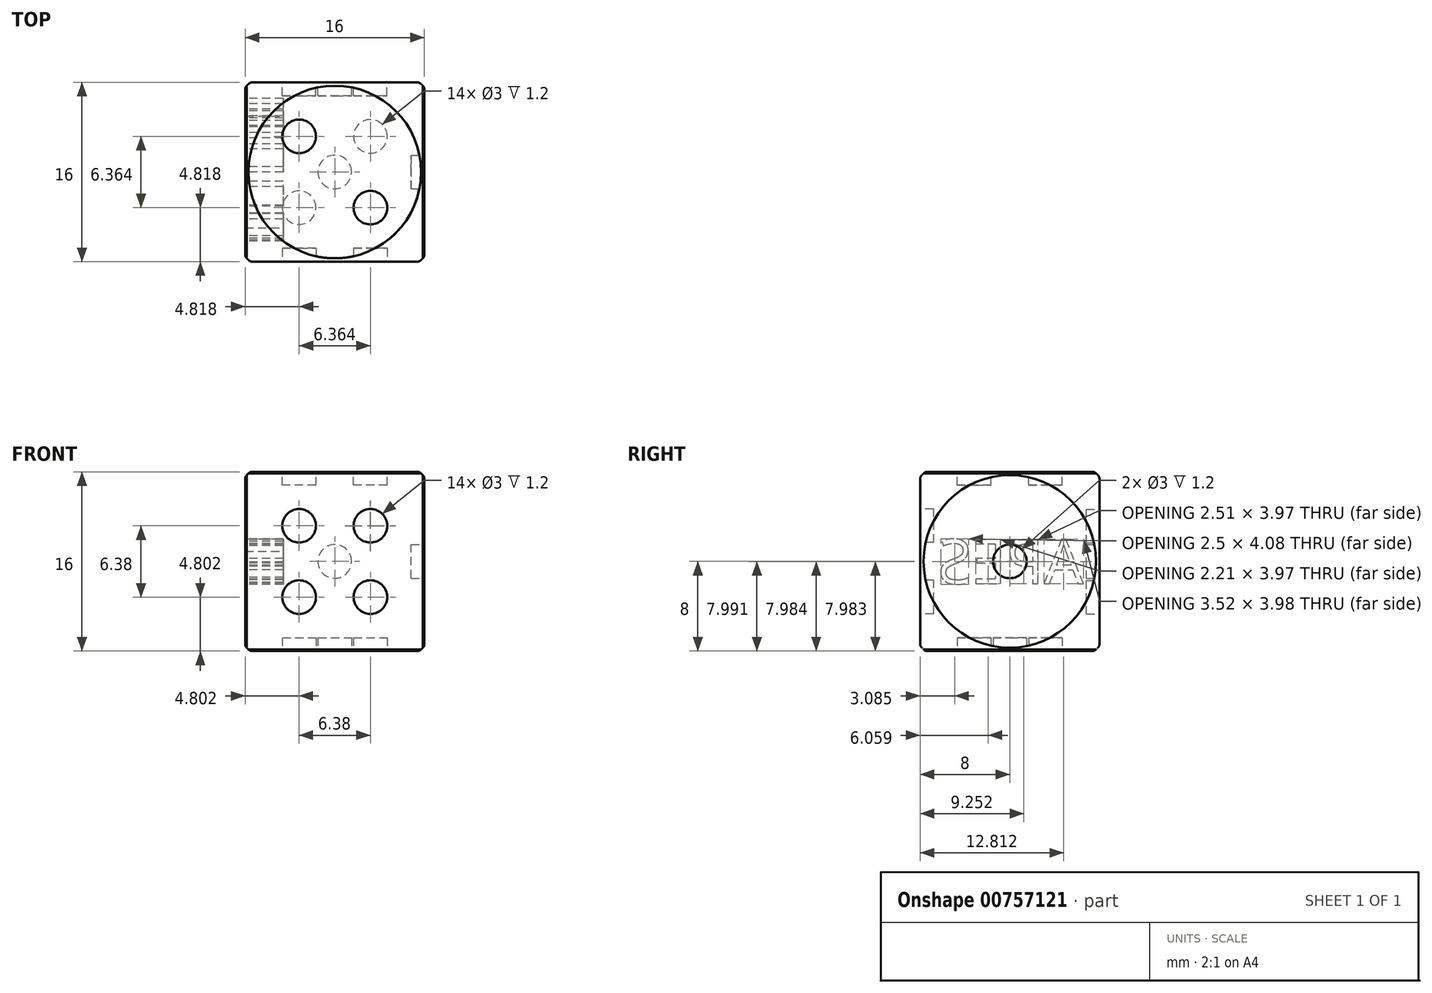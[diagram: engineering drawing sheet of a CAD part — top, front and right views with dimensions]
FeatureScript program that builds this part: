
annotation { "Feature Type Name" : "Feature", "Feature Type Description" : "" }
export const myFeature = defineFeature(function(context is Context, id is Id, definition is map)
    precondition{}
    {
        {
            var Q0;
            Q0=qCreatedBy(makeId("Top.planeOp"),FACE);
            var sketch = newSketch(context, id + "F0", { "sketchPlane" : qUnion([Q0])});
            skLineSegment(sketch, "E0.bottom", {"start": v(-8, 8) * mm, "end": v(8, 8) * mm});
            skLineSegment(sketch, "E0.top", {"start": v(-8, -8) * mm, "end": v(8, -8) * mm});
            skLineSegment(sketch, "E0.left", {"start": v(-8, 8) * mm, "end": v(-8, -8) * mm});
            skLineSegment(sketch, "E0.right", {"start": v(8, 8) * mm, "end": v(8, -8) * mm});
            skSolve(sketch);
        }
        {
            var Q0;
            Q0=makeQuery(id+"F0.imprint","IMPRINT",FACE,{"disambiguationData":[TD([[makeQuery(id+"F0.imprint","IMPRINT",EDGE,{"derivedFrom":sQuery(id+"F0.wireOp",EDGE,"E0.bottom")}),-1.0]])]});
            extrude(context, id + "F1", {"entities" : qUnion([Q0]), "endBound" : BoundingType.SYMMETRIC, "depth" : 16 * mm, "offsetDistance" : 25 * mm});
        }
        {
            var Q0;
            Q0=qCreatedBy(makeId("Top.planeOp"),FACE);
            var sketch = newSketch(context, id + "F2", { "sketchPlane" : qUnion([Q0])});
            skArc(sketch, "E1", {"start": v(0, 11) * mm, "mid": v(-11, 0) * mm, "end": v(0, -11) * mm});
            skLineSegment(sketch, "E2", {"start": v(0, 11) * mm, "end": v(0, 18.89) * mm});
            skArc(sketch, "E3", {"start": v(0, 18.89) * mm, "mid": v(-18.89, 0) * mm, "end": v(0, -18.89) * mm});
            skLineSegment(sketch, "E4", {"start": v(0, -11) * mm, "end": v(0, -18.89) * mm});
            skLineSegment(sketch, "E5", {"start": v(0, 33.4) * mm, "end": v(0, -38.28) * mm, "construction": true});
            skSolve(sketch);
        }
        {
            var Q0;
            Q0=makeQuery(id+"F2.imprint","IMPRINT",FACE,{"disambiguationData":[TD([[makeQuery(id+"F2.imprint","IMPRINT",EDGE,{"derivedFrom":sQuery(id+"F2.wireOp",EDGE,"E1")}),-1.0]])]});
            var Q1;
            Q1=sQuery(id+"F2.wireOp",EDGE,"E5");
            revolve(context, id + "F3", {"operationType" : NewBodyOperationType.REMOVE, "surfaceOperationType" : NewSurfaceOperationType.NEW, "entities" : qUnion([Q0]), "axis" : qUnion([Q1]), "revolveType" : RevolveType.FULL});
        }
        {
            var Q0;
            Q0=makeQuery(id+"F1.opExtrude","CAP_FACE",FACE,{"disambiguationData":[OSD([sQuery(id+"F0.wireOp",EDGE,"E0.bottom"),sQuery(id+"F0.wireOp",EDGE,"E0.top"),sQuery(id+"F0.wireOp",EDGE,"E0.left"),sQuery(id+"F0.wireOp",EDGE,"E0.right")])],"isStart":false});
            var Q1;
            Q1=makeQuery(id+"F1.opExtrude","SWEPT_FACE",FACE,{"disambiguationData":[OSD([sQuery(id+"F0.wireOp",EDGE,"E0.top")])]});
            var Q2;
            Q2=makeQuery(id+"F1.opExtrude","SWEPT_FACE",FACE,{"disambiguationData":[OSD([sQuery(id+"F0.wireOp",EDGE,"E0.left")])]});
            var Q3;
            Q3=makeQuery(id+"F1.opExtrude","SWEPT_FACE",FACE,{"disambiguationData":[OSD([sQuery(id+"F0.wireOp",EDGE,"E0.right")])]});
            var Q4;
            Q4=makeQuery(id+"F1.opExtrude","SWEPT_FACE",FACE,{"disambiguationData":[OSD([sQuery(id+"F0.wireOp",EDGE,"E0.bottom")])]});
            var Q5;
            Q5=makeQuery(id+"F1.opExtrude","CAP_FACE",FACE,{"disambiguationData":[OSD([sQuery(id+"F0.wireOp",EDGE,"E0.bottom"),sQuery(id+"F0.wireOp",EDGE,"E0.top"),sQuery(id+"F0.wireOp",EDGE,"E0.left"),sQuery(id+"F0.wireOp",EDGE,"E0.right")])],"isStart":true});
            fillet(context, id + "F4", {"entities" : qUnion([Q0, Q1, Q2, Q3, Q4, Q5]), "radius" : 0.5 * mm, "tangentPropagation" : true, "allowEdgeOverflow" : false});
        }
        {
            var Q0;
            Q0=makeQuery(id+"F1.opExtrude","CAP_FACE",FACE,{"disambiguationData":[OSD([sQuery(id+"F0.wireOp",EDGE,"E0.bottom"),sQuery(id+"F0.wireOp",EDGE,"E0.top"),sQuery(id+"F0.wireOp",EDGE,"E0.left"),sQuery(id+"F0.wireOp",EDGE,"E0.right")])],"isStart":false});
            var sketch = newSketch(context, id + "F5", { "sketchPlane" : qUnion([Q0])});
            skLineSegment(sketch, "E6", {"start": v(-6.8, 6.8) * mm, "end": v(0, 0) * mm, "construction": true});
            skLineSegment(sketch, "E7", {"start": v(0, 0) * mm, "end": v(6.37, -6.37) * mm, "construction": true});
            skCircle(sketch, "E8", {"center": v(-3.18, 3.18) * mm, "radius": 1.5 * mm});
            skCircle(sketch, "E9", {"center": v(3.18, -3.18) * mm, "radius": 1.5 * mm});
            skSolve(sketch);
        }
        {
            var Q0;
            Q0 = qSketchRegion(id + "F5", true);
            extrude(context, id + "F6", {"entities" : qUnion([Q0]), "operationType" : NewBodyOperationType.REMOVE, "oppositeDirection" : true, "depth" : 1.2 * mm, "offsetDistance" : 25 * mm});
        }
        {
            var Q0;
            Q0=makeQuery(id+"F1.opExtrude","SWEPT_FACE",FACE,{"disambiguationData":[OSD([sQuery(id+"F0.wireOp",EDGE,"E0.right")])]});
            var sketch = newSketch(context, id + "F7", { "sketchPlane" : qUnion([Q0])});
            skCircle(sketch, "E10", {"center": v(0, 0) * mm, "radius": 1.5 * mm});
            skSolve(sketch);
        }
        {
            var Q0;
            Q0 = qSketchRegion(id + "F7", true);
            extrude(context, id + "F8", {"entities" : qUnion([Q0]), "operationType" : NewBodyOperationType.REMOVE, "oppositeDirection" : true, "depth" : 1.2 * mm, "offsetDistance" : 25 * mm});
        }
        {
            var Q0;
            Q0=makeQuery(id+"F1.opExtrude","CAP_FACE",FACE,{"disambiguationData":[OSD([sQuery(id+"F0.wireOp",EDGE,"E0.bottom"),sQuery(id+"F0.wireOp",EDGE,"E0.top"),sQuery(id+"F0.wireOp",EDGE,"E0.left"),sQuery(id+"F0.wireOp",EDGE,"E0.right")])],"isStart":true});
            var sketch = newSketch(context, id + "F9", { "sketchPlane" : qUnion([Q0])});
            skLineSegment(sketch, "E11", {"start": v(0, 0) * mm, "end": v(-3.18, 3.18) * mm, "construction": true});
            skLineSegment(sketch, "E12", {"start": v(0, 0) * mm, "end": v(3.18, -3.18) * mm, "construction": true});
            skLineSegment(sketch, "E13", {"start": v(0, 0) * mm, "end": v(3.18, 3.18) * mm, "construction": true});
            skLineSegment(sketch, "E14", {"start": v(0, 0) * mm, "end": v(-3.18, -3.18) * mm, "construction": true});
            skCircle(sketch, "E15", {"center": v(-3.18, 3.18) * mm, "radius": 1.5 * mm});
            skCircle(sketch, "E16", {"center": v(3.18, 3.18) * mm, "radius": 1.5 * mm});
            skCircle(sketch, "E17", {"center": v(-3.18, -3.18) * mm, "radius": 1.5 * mm});
            skCircle(sketch, "E18", {"center": v(3.18, -3.18) * mm, "radius": 1.5 * mm});
            skCircle(sketch, "E19", {"center": v(0, 0) * mm, "radius": 1.5 * mm});
            skSolve(sketch);
        }
        {
            var Q0;
            Q0=makeQuery(id+"F9.imprint","IMPRINT",FACE,{"disambiguationData":[TD([[makeQuery(id+"F9.imprint","IMPRINT",EDGE,{"derivedFrom":sQuery(id+"F9.wireOp",EDGE,"E15")}),1.0]])]});
            var Q1;
            Q1=makeQuery(id+"F9.imprint","IMPRINT",FACE,{"disambiguationData":[TD([[makeQuery(id+"F9.imprint","IMPRINT",EDGE,{"derivedFrom":sQuery(id+"F9.wireOp",EDGE,"E19")}),1.0]])]});
            var Q2;
            Q2=makeQuery(id+"F9.imprint","IMPRINT",FACE,{"disambiguationData":[TD([[makeQuery(id+"F9.imprint","IMPRINT",EDGE,{"derivedFrom":sQuery(id+"F9.wireOp",EDGE,"E16")}),1.0]])]});
            var Q3;
            Q3=makeQuery(id+"F9.imprint","IMPRINT",FACE,{"disambiguationData":[TD([[makeQuery(id+"F9.imprint","IMPRINT",EDGE,{"derivedFrom":sQuery(id+"F9.wireOp",EDGE,"E18")}),1.0]])]});
            var Q4;
            Q4=makeQuery(id+"F9.imprint","IMPRINT",FACE,{"disambiguationData":[TD([[makeQuery(id+"F9.imprint","IMPRINT",EDGE,{"derivedFrom":sQuery(id+"F9.wireOp",EDGE,"E17")}),1.0]])]});
            var Q5;
            Q5=sQuery(id+"F9.wireOp",EDGE,"E15");
            var Q6;
            Q6=sQuery(id+"F9.wireOp",EDGE,"E19");
            var Q7;
            Q7=sQuery(id+"F9.wireOp",EDGE,"E16");
            var Q8;
            Q8=sQuery(id+"F9.wireOp",EDGE,"E18");
            var Q9;
            Q9=sQuery(id+"F9.wireOp",EDGE,"E17");
            extrude(context, id + "F10", {"entities" : qUnion([Q0, Q1, Q2, Q3, Q4]), "operationType" : NewBodyOperationType.REMOVE, "surfaceEntities" : qUnion([Q5, Q6, Q7, Q8, Q9]), "oppositeDirection" : true, "depth" : 1.2 * mm, "offsetDistance" : 25 * mm});
        }
        {
            var Q0;
            Q0=makeQuery(id+"F1.opExtrude","SWEPT_FACE",FACE,{"disambiguationData":[OSD([sQuery(id+"F0.wireOp",EDGE,"E0.top")])]});
            var sketch = newSketch(context, id + "F11", { "sketchPlane" : qUnion([Q0])});
            skCircle(sketch, "E20", {"center": v(0, 0) * mm, "radius": 4.5 * mm, "construction": true});
            skLineSegment(sketch, "E21", {"start": v(-4.77, 4.77) * mm, "end": v(4.83, -4.83) * mm, "construction": true});
            skLineSegment(sketch, "E22", {"start": v(4.67, 4.67) * mm, "end": v(-4.7, -4.7) * mm, "construction": true});
            skCircle(sketch, "E23", {"center": v(-3.18, 3.18) * mm, "radius": 1.5 * mm});
            skCircle(sketch, "E24", {"center": v(3.18, 3.18) * mm, "radius": 1.5 * mm});
            skCircle(sketch, "E25", {"center": v(3.18, -3.18) * mm, "radius": 1.5 * mm});
            skCircle(sketch, "E26", {"center": v(-3.18, -3.18) * mm, "radius": 1.5 * mm});
            skSolve(sketch);
        }
        {
            var Q0;
            Q0=makeQuery(id+"F11.imprint","IMPRINT",FACE,{"disambiguationData":[TD([[makeQuery(id+"F11.imprint","IMPRINT",EDGE,{"derivedFrom":sQuery(id+"F11.wireOp",EDGE,"E23")}),1.0]])]});
            var Q1;
            Q1=makeQuery(id+"F11.imprint","IMPRINT",FACE,{"disambiguationData":[TD([[makeQuery(id+"F11.imprint","IMPRINT",EDGE,{"derivedFrom":sQuery(id+"F11.wireOp",EDGE,"E24")}),1.0]])]});
            var Q2;
            Q2=makeQuery(id+"F11.imprint","IMPRINT",FACE,{"disambiguationData":[TD([[makeQuery(id+"F11.imprint","IMPRINT",EDGE,{"derivedFrom":sQuery(id+"F11.wireOp",EDGE,"E25")}),1.0]])]});
            var Q3;
            Q3=makeQuery(id+"F11.imprint","IMPRINT",FACE,{"disambiguationData":[TD([[makeQuery(id+"F11.imprint","IMPRINT",EDGE,{"derivedFrom":sQuery(id+"F11.wireOp",EDGE,"E26")}),1.0]])]});
            extrude(context, id + "F12", {"entities" : qUnion([Q0, Q1, Q2, Q3]), "operationType" : NewBodyOperationType.REMOVE, "oppositeDirection" : true, "depth" : 1.2 * mm, "offsetDistance" : 25 * mm});
        }
        {
            var Q0;
            Q0=makeQuery(id+"F1.opExtrude","SWEPT_FACE",FACE,{"disambiguationData":[OSD([sQuery(id+"F0.wireOp",EDGE,"E0.bottom")])]});
            var sketch = newSketch(context, id + "F13", { "sketchPlane" : qUnion([Q0])});
            skLineSegment(sketch, "E27", {"start": v(-3.17, 3.17) * mm, "end": v(3.2, -3.2) * mm, "construction": true});
            skCircle(sketch, "E28", {"center": v(-3.17, 3.17) * mm, "radius": 1.5 * mm});
            skCircle(sketch, "E29", {"center": v(3.2, -3.2) * mm, "radius": 1.5 * mm});
            skCircle(sketch, "E30", {"center": v(0, 0) * mm, "radius": 1.5 * mm});
            skSolve(sketch);
        }
        {
            var Q0;
            Q0=makeQuery(id+"F13.imprint","IMPRINT",FACE,{"disambiguationData":[TD([[makeQuery(id+"F13.imprint","IMPRINT",EDGE,{"derivedFrom":sQuery(id+"F13.wireOp",EDGE,"E28")}),1.0]])]});
            var Q1;
            Q1=makeQuery(id+"F13.imprint","IMPRINT",FACE,{"disambiguationData":[TD([[makeQuery(id+"F13.imprint","IMPRINT",EDGE,{"derivedFrom":sQuery(id+"F13.wireOp",EDGE,"E30")}),1.0]])]});
            var Q2;
            Q2=makeQuery(id+"F13.imprint","IMPRINT",FACE,{"disambiguationData":[TD([[makeQuery(id+"F13.imprint","IMPRINT",EDGE,{"derivedFrom":sQuery(id+"F13.wireOp",EDGE,"E29")}),1.0]])]});
            extrude(context, id + "F14", {"entities" : qUnion([Q0, Q1, Q2]), "operationType" : NewBodyOperationType.REMOVE, "oppositeDirection" : true, "depth" : 1.2 * mm, "offsetDistance" : 25 * mm});
        }
        {
            var Q0;
            Q0=makeQuery(id+"F1.opExtrude","SWEPT_FACE",FACE,{"disambiguationData":[OSD([sQuery(id+"F0.wireOp",EDGE,"E0.left")])]});
            var sketch = newSketch(context, id + "F15", { "sketchPlane" : qUnion([Q0])});
            skText(sketch, "E31", { "text": "APES", "fontName": "OpenSans-Regular.ttf"});
            const initialGuessF15  = {"E31": [-0.00657, -0.002, 1, 0, 0.004]};
            skSetInitialGuess(sketch, initialGuessF15);
            skSolve(sketch);
        }
        {
            var Q0;
            Q0=makeQuery(id+"F15.imprint","IMPRINT",FACE,{"disambiguationData":[TD([[makeQuery(id+"F15.imprint","IMPRINT",EDGE,{"derivedFrom":sQuery(id+"F15.wireOp",EDGE,"E31.sketch_text.stroke-0")}),-1.0]])]});
            var Q1;
            Q1=makeQuery(id+"F15.imprint","IMPRINT",FACE,{"disambiguationData":[TD([[makeQuery(id+"F15.imprint","IMPRINT",EDGE,{"derivedFrom":sQuery(id+"F15.wireOp",EDGE,"E31.sketch_text.stroke-13")}),-1.0]])]});
            var Q2;
            Q2=makeQuery(id+"F15.imprint","IMPRINT",FACE,{"disambiguationData":[TD([[makeQuery(id+"F15.imprint","IMPRINT",EDGE,{"derivedFrom":sQuery(id+"F15.wireOp",EDGE,"E31.sketch_text.stroke-28")}),-1.0]])]});
            var Q3;
            Q3=makeQuery(id+"F15.imprint","IMPRINT",FACE,{"disambiguationData":[TD([[makeQuery(id+"F15.imprint","IMPRINT",EDGE,{"derivedFrom":sQuery(id+"F15.wireOp",EDGE,"E31.sketch_text.stroke-40")}),-1.0]])]});
            extrude(context, id + "F16", {"entities" : qUnion([Q0, Q1, Q2, Q3]), "operationType" : NewBodyOperationType.REMOVE, "oppositeDirection" : true, "depth" : 3.4 * mm, "offsetDistance" : 25 * mm});
        }
    });
